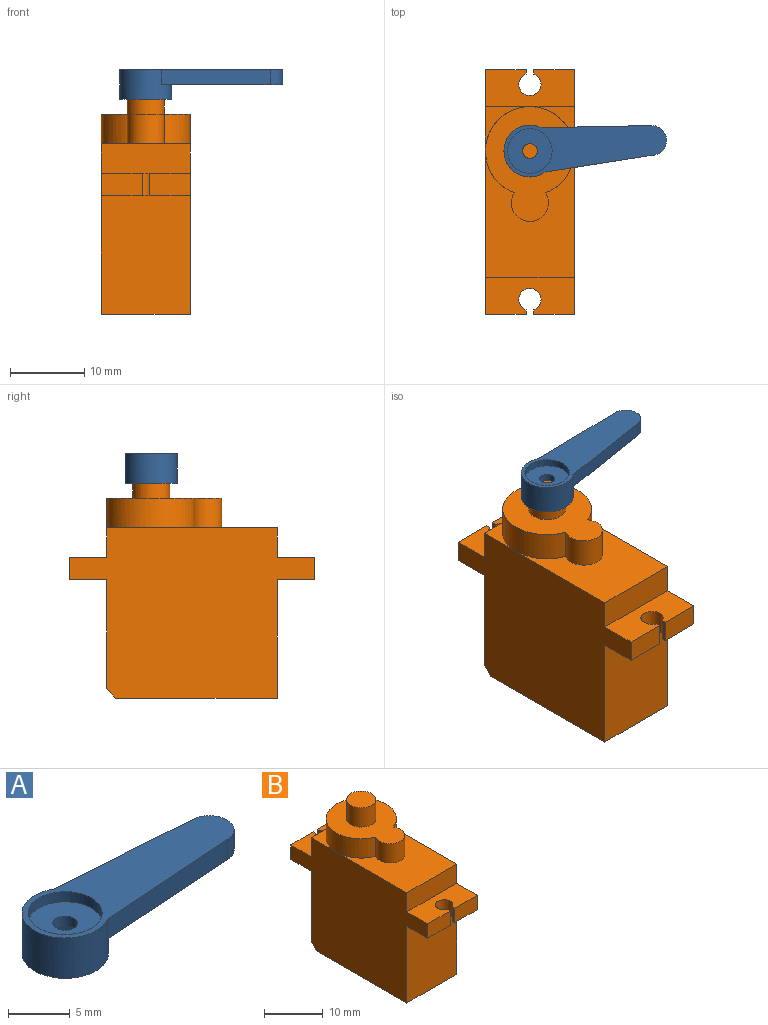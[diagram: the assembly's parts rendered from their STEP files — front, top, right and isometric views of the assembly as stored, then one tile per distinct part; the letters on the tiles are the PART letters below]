
ASSEMBLY  parts=2 mates=1
PART A: 12 faces, bbox 22x7x4 mm
  f0: plane 14.83x2mm, normal (0.07,1,0), area 29.7mm2, adj f1,f3,f4,f5
  f1: cylinder r=3.5mm len=7mm, axis (0,0,-1), area 73.5mm2, adj f0,f2,f4,f5,f6
  f2: plane 14.83x2mm, normal (0.07,-1,0), area 29.7mm2, adj f1,f3,f4,f5
  f3: cylinder r=2mm len=3.99mm, axis (0,0,-1), area 12mm2, adj f0,f2,f4,f5
  f4: plane 22x7mm, normal (0,0,1), area 82.8mm2, adj f0,f1,f2,f3,f9
  f5: plane 16.7x6mm, normal (0,0,-1), area 72.6mm2, adj f0,f1,f2,f3
  f6: plane 7x7mm, normal (0,0,-1), area 18.8mm2, adj f1,f7
  f7: cylinder r=2.5mm len=5mm, axis (0,0,-1), area 31.4mm2, adj f6,f8
  f8: plane 5x5mm, normal (0,0,-1), area 16.5mm2, adj f7,f11
  f9: cylinder r=3mm len=6mm, axis (0,0,1), area 18.8mm2, adj f4,f10
  f10: plane 6x6mm, normal (0,0,1), area 25.1mm2, adj f9,f11
  f11: cylinder r=1mm len=2mm, axis (0,0,1), area 6.3mm2, adj f8,f10
PART B: 30 faces, bbox 12x33x31 mm
  f0: plane 14.65x12mm, normal (0,1,0), area 175.8mm2, adj f9,f16,f17,f29
  f1: plane 17x12mm, normal (0,0,1), area 132.2mm2, adj f13,f16,f17,f24,f25
  f2: plane 6x6mm, normal (0,0,1), area 7.7mm2, adj f11,f16,f24
  f3: plane 5.5x3mm, normal (0,-1,0), area 16.5mm2, adj f4,f15,f16,f21
  f4: plane 12x5mm, normal (0,0,1), area 52.4mm2, adj f3,f13,f14,f16,f17,f21,f22,f23
  f5: plane 5.5x3mm, normal (0,1,0), area 16.5mm2, adj f6,f9,f17,f18
  f6: plane 12x5mm, normal (0,0,1), area 52.4mm2, adj f5,f10,f11,f16,f17,f18,f19,f20
  f7: plane 16x12mm, normal (0,-1,0), area 192mm2, adj f8,f15,f16,f17
  f8: plane 21.81x12mm, normal (0,0,-1), area 261.7mm2, adj f7,f16,f17,f29
  f9: plane 12x5mm, normal (0,0,-1), area 52.4mm2, adj f0,f5,f10,f16,f17,f18,f19,f20
  f10: plane 5.5x3mm, normal (0,1,0), area 16.5mm2, adj f6,f9,f16,f19
  f11: plane 12x4mm, normal (0,1,0), area 48mm2, adj f2,f6,f12,f16,f17
  f12: plane 6x6mm, normal (0,0,1), area 7.7mm2, adj f11,f17,f24
  f13: plane 12x4mm, normal (0,-1,0), area 48mm2, adj f1,f4,f16,f17
  f14: plane 5.5x3mm, normal (0,-1,0), area 16.5mm2, adj f4,f15,f17,f23
  f15: plane 12x5mm, normal (0,0,-1), area 52.4mm2, adj f3,f7,f14,f16,f17,f21,f22,f23
  f16: plane 33x23mm, normal (1,0,0), area 558.2mm2, adj f0,f1,f2,f3,f4,f6,f7,f8
  f17: plane 33x23mm, normal (-1,0,0), area 558.2mm2, adj f0,f1,f4,f5,f6,f7,f8,f9
  f18: plane 3x0.59mm, normal (1,0,0), area 1.8mm2, adj f5,f6,f9,f20
  f19: plane 3x0.59mm, normal (-1,0,0), area 1.8mm2, adj f6,f9,f10,f20
  f20: cylinder r=1.5mm len=3mm, axis (0,0,1), area 25.2mm2, adj f6,f9,f18,f19
  f21: plane 3x0.59mm, normal (-1,0,0), area 1.8mm2, adj f3,f4,f15,f22
  f22: cylinder r=1.5mm len=3mm, axis (0,0,1), area 25.2mm2, adj f4,f15,f21,f23
  f23: plane 3x0.59mm, normal (1,0,0), area 1.8mm2, adj f4,f14,f15,f22
  f24: cylinder r=6mm len=12mm, axis (0,0,-1), area 133.7mm2, adj f1,f2,f12,f25,f26
  f25: cylinder r=2.5mm len=5mm, axis (0,0,-1), area 43.1mm2, adj f1,f24,f26
  f26: plane 15.5x12mm, normal (0,0,1), area 108.7mm2, adj f24,f25,f27
  f27: cylinder r=2.5mm len=5mm, axis (0,0,-1), area 62.8mm2, adj f26,f28
  f28: plane 5x5mm, normal (0,0,1), area 19.6mm2, adj f27
  f29: plane 12x1.35mm, normal (0,0.75,-0.66), area 21.6mm2, adj f0,f8,f16,f17
PLACE A rot(axis=(0,0,1),5deg) t=(-14.56,-15.22,18.73)mm
PLACE B t=(-14.17,-14.65,18.63)mm
MATE revolute A.f1 <-> B.f24  axis (0,0,-1) through (-8.17,-20.17,30.63)mm
